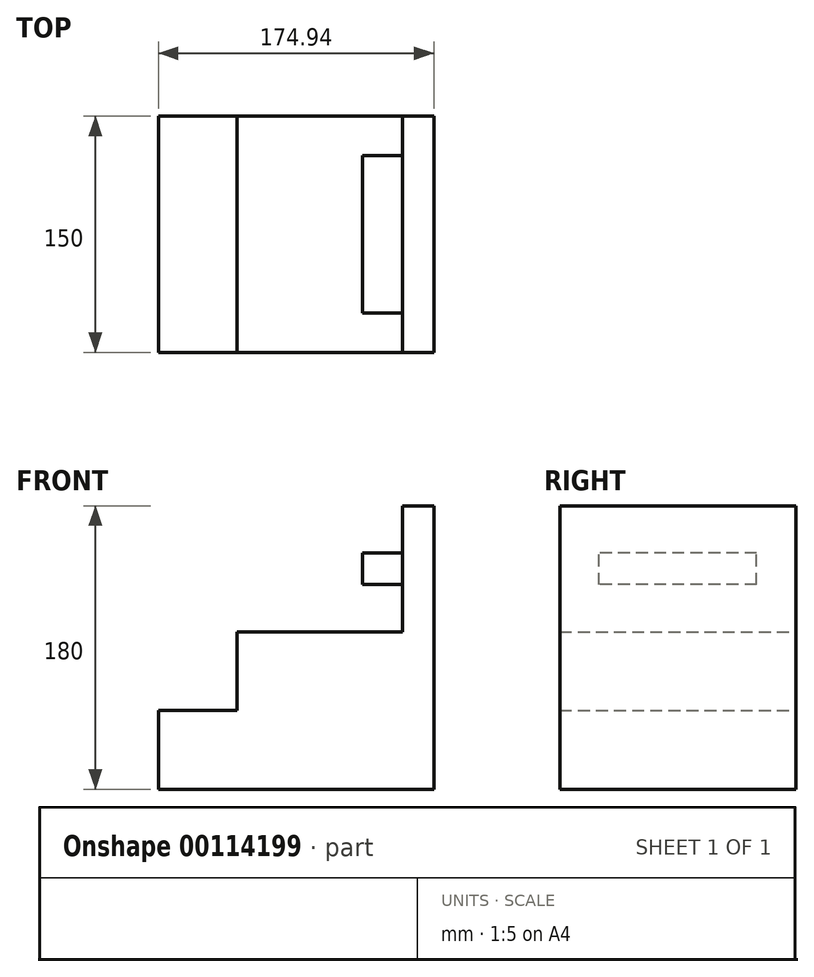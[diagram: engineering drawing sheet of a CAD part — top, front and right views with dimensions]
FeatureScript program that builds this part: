
annotation { "Feature Type Name" : "Feature", "Feature Type Description" : "" }
export const myFeature = defineFeature(function(context is Context, id is Id, definition is map)
    precondition{}
    {
        {
            var Q0;
            Q0=qCreatedBy(makeId("Front.planeOp"),FACE);
            var sketch = newSketch(context, id + "F0", { "sketchPlane" : qUnion([Q0])});
            skLineSegment(sketch, "E0.top", {"start": v(67.47, 90) * mm, "end": v(87.47, 90) * mm});
            skPoint(sketch, "E0.middle", {"position": v(0, 0) * mm});
            skLineSegment(sketch, "E1", {"start": v(67.47, 90) * mm, "end": v(67.47, 10) * mm});
            skLineSegment(sketch, "E2", {"start": v(67.47, 10) * mm, "end": v(-37.47, 10) * mm});
            skLineSegment(sketch, "E3", {"start": v(-37.47, 10) * mm, "end": v(-37.47, -40) * mm});
            skLineSegment(sketch, "E4", {"start": v(-37.47, -40) * mm, "end": v(-87.47, -40) * mm});
            skPoint(sketch, "E5.orphan", {"position": v(-87.47, 90) * mm});
            skPoint(sketch, "E6.orphan", {"position": v(87.47, -90) * mm});
            skPoint(sketch, "E7.orphan", {"position": v(-87.47, -90) * mm});
            skLineSegment(sketch, "E8", {"start": v(-87.47, -90) * mm, "end": v(87.47, -90) * mm});
            skLineSegment(sketch, "E9", {"start": v(-87.47, -40) * mm, "end": v(-87.47, -90) * mm});
            skLineSegment(sketch, "E10", {"start": v(87.47, 90) * mm, "end": v(87.47, -90) * mm});
            skSolve(sketch);
        }
        {
            var Q0;
            Q0 = qSketchRegion(id + "F0", true);
            extrude(context, id + "F1", {"entities" : qUnion([Q0]), "depth" : 150 * mm});
        }
        {
            var Q0;
            Q0=makeQuery(id+"F1.opExtrude","SWEPT_FACE",FACE,{"disambiguationData":[OSD([sQuery(id+"F0.wireOp",EDGE,"E1")])]});
            var sketch = newSketch(context, id + "F2", { "sketchPlane" : qUnion([Q0])});
            skLineSegment(sketch, "E11.bottom", {"start": v(25, 40) * mm, "end": v(125, 40) * mm});
            skLineSegment(sketch, "E11.top", {"start": v(25, 60) * mm, "end": v(125, 60) * mm});
            skLineSegment(sketch, "E11.left", {"start": v(25, 40) * mm, "end": v(25, 60) * mm});
            skLineSegment(sketch, "E11.right", {"start": v(125, 40) * mm, "end": v(125, 60) * mm});
            skSolve(sketch);
        }
        {
            var Q0;
            Q0 = qSketchRegion(id + "F2", true);
            extrude(context, id + "F3", {"entities" : qUnion([Q0]), "operationType" : NewBodyOperationType.ADD, "depth" : 25.4 * mm});
        }
    });
